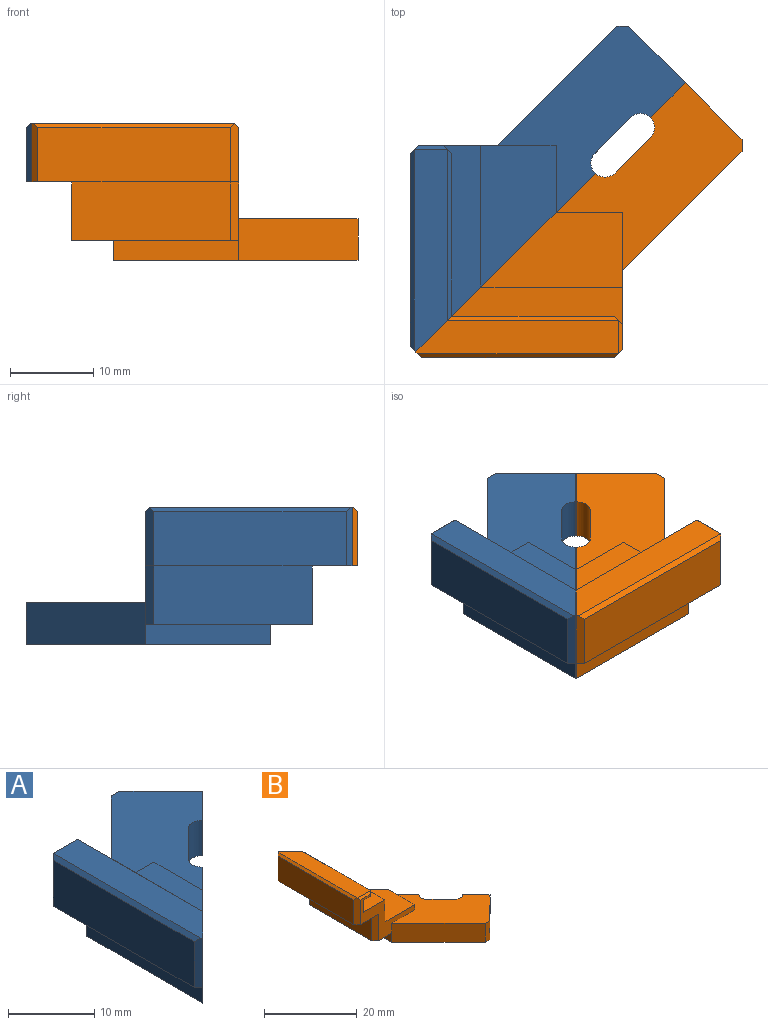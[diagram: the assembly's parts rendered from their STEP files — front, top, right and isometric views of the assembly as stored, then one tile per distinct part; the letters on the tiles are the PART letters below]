
ASSEMBLY  parts=2 mates=1
PART A: 31 faces, bbox 33x39.1x16.4 mm
  f0: plane 20x5mm, normal (0,0,-1), area 87mm2, adj f12,f17,f18,f22,f24
  f1: plane 22.5x22.29mm, normal (0,0,1), area 185.5mm2, adj f2,f14,f15,f16,f17,f19,f20,f21
  f2: plane 8x1.4mm, normal (1,0,0), area 11.2mm2, adj f1,f3,f17,f22
  f3: plane 17x9mm, normal (0,0,1), area 112.5mm2, adj f2,f4,f17,f22
  f4: plane 17x5.8mm, normal (1,0,0), area 98.6mm2, adj f3,f5,f17,f22
  f5: plane 23.5x6.5mm, normal (0,0,1), area 131.6mm2, adj f4,f6,f17,f22
  f6: plane 23.5x3.2mm, normal (1,0,0), area 75.2mm2, adj f5,f7,f17,f22
  f7: plane 23.5x3mm, normal (0,0,-1), area 65.5mm2, adj f6,f8,f17,f22,f23
  f8: plane 19.5x0.5mm, normal (1,0,0), area 9.8mm2, adj f7,f22,f23,f29
  f9: plane 24.29x4mm, normal (0,0,1), area 90mm2, adj f22,f27,f28,f29,f30
  f10: plane 23.09x6.5mm, normal (-1,0,0), area 150.1mm2, adj f11,f25,f28,f30
  f11: plane 24.79x6.5mm, normal (0,0,-1), area 124.6mm2, adj f10,f12,f17,f22,f24,f25,f30
  f12: plane 19x7mm, normal (-1,0,0), area 133mm2, adj f0,f11,f22,f24
  f13: plane 29.29x22.5mm, normal (0,0,-1), area 266mm2, adj f14,f15,f16,f18,f19,f20,f21,f22
  f14: plane 6.79x6.79mm, normal (0.71,0.71,0), area 48mm2, adj f1,f13,f21,f26
  f15: cylinder r=1.7mm len=5mm, axis (0,0,1), area 13.4mm2, adj f1,f13,f20,f22
  f16: cylinder r=1.7mm len=5mm, axis (0,0,1), area 13.4mm2, adj f1,f13,f20,f21
  f17: plane 16.5x13.5mm, normal (0,1,0), area 57.5mm2, adj f0,f1,f2,f3,f4,f5,f6,f7
  f18: plane 15x2.4mm, normal (-1,0,0), area 36mm2, adj f0,f13,f19,f22
  f19: plane 14.29x14.29mm, normal (-0.71,0.71,0), area 101.1mm2, adj f1,f13,f17,f18,f26
  f20: plane 5x4.24mm, normal (0.71,-0.71,0), area 30mm2, adj f1,f13,f15,f16
  f21: plane 5x4.18mm, normal (0.71,-0.71,0), area 29.5mm2, adj f1,f13,f14,f16
  f22: plane 21.47x21.47mm, normal (0.71,-0.71,0), area 180mm2, adj f0,f1,f2,f3,f4,f5,f6,f7
  f23: plane 1x1mm, normal (0.71,0.71,0), area 1.1mm2, adj f7,f8,f17,f27,f29
  f24: plane 7x1mm, normal (-0.71,0.71,0), area 9.9mm2, adj f0,f11,f12,f17
  f25: plane 7x1mm, normal (-0.71,0.71,0), area 9.5mm2, adj f10,f11,f17,f27,f28
  f26: plane 5x1.41mm, normal (0,1,0), area 7.1mm2, adj f1,f13,f14,f19
  f27: plane 4x0.5mm, normal (0,0.71,0.71), area 2.5mm2, adj f9,f17,f23,f25
  f28: plane 24.09x0.5mm, normal (-0.71,0,0.71), area 16.7mm2, adj f9,f10,f25,f30
  f29: plane 20.5x0.5mm, normal (0.71,0,0.71), area 14.1mm2, adj f8,f9,f22,f23
  f30: plane 7x0.71mm, normal (-0.71,-0.71,0), area 6.8mm2, adj f9,f10,f11,f22,f28
PART B: 31 faces, bbox 33x39.1x16.4 mm
  f0: plane 20x5mm, normal (0,0,-1), area 87mm2, adj f12,f17,f18,f22,f24
  f1: plane 22.5x22.29mm, normal (0,0,1), area 185.5mm2, adj f2,f14,f15,f16,f17,f19,f20,f21
  f2: plane 8x1.4mm, normal (1,0,0), area 11.2mm2, adj f1,f3,f17,f22
  f3: plane 17x9mm, normal (0,0,1), area 112.5mm2, adj f2,f4,f17,f22
  f4: plane 17x5.8mm, normal (1,0,0), area 98.6mm2, adj f3,f5,f17,f22
  f5: plane 23.5x6.5mm, normal (0,0,1), area 131.6mm2, adj f4,f6,f17,f22
  f6: plane 23.5x3.2mm, normal (1,0,0), area 75.2mm2, adj f5,f7,f17,f22
  f7: plane 23.5x3mm, normal (0,0,-1), area 65.5mm2, adj f6,f8,f17,f22,f23
  f8: plane 19.5x0.5mm, normal (1,0,0), area 9.8mm2, adj f7,f22,f23,f29
  f9: plane 24.29x4mm, normal (0,0,1), area 90mm2, adj f22,f27,f28,f29,f30
  f10: plane 23.09x6.5mm, normal (-1,0,0), area 150.1mm2, adj f11,f25,f28,f30
  f11: plane 24.79x6.5mm, normal (0,0,-1), area 124.6mm2, adj f10,f12,f17,f22,f24,f25,f30
  f12: plane 19x7mm, normal (-1,0,0), area 133mm2, adj f0,f11,f22,f24
  f13: plane 29.29x22.5mm, normal (0,0,-1), area 266mm2, adj f14,f15,f16,f18,f19,f20,f21,f22
  f14: plane 6.79x6.79mm, normal (0.71,-0.71,0), area 48mm2, adj f1,f13,f21,f26
  f15: cylinder r=1.7mm len=5mm, axis (0,0,1), area 13.4mm2, adj f1,f13,f20,f22
  f16: cylinder r=1.7mm len=5mm, axis (0,0,1), area 13.4mm2, adj f1,f13,f20,f21
  f17: plane 16.5x13.5mm, normal (0,-1,0), area 57.5mm2, adj f0,f1,f2,f3,f4,f5,f6,f7
  f18: plane 15x2.4mm, normal (-1,0,0), area 36mm2, adj f0,f13,f19,f22
  f19: plane 14.29x14.29mm, normal (-0.71,-0.71,0), area 101.1mm2, adj f1,f13,f17,f18,f26
  f20: plane 5x4.24mm, normal (0.71,0.71,0), area 30mm2, adj f1,f13,f15,f16
  f21: plane 5x4.18mm, normal (0.71,0.71,0), area 29.5mm2, adj f1,f13,f14,f16
  f22: plane 21.47x21.47mm, normal (0.71,0.71,0), area 180mm2, adj f0,f1,f2,f3,f4,f5,f6,f7
  f23: plane 1x1mm, normal (0.71,-0.71,0), area 1.1mm2, adj f7,f8,f17,f27,f29
  f24: plane 7x1mm, normal (-0.71,-0.71,0), area 9.9mm2, adj f0,f11,f12,f17
  f25: plane 7x1mm, normal (-0.71,-0.71,0), area 9.5mm2, adj f10,f11,f17,f27,f28
  f26: plane 5x1.41mm, normal (0,-1,0), area 7.1mm2, adj f1,f13,f14,f19
  f27: plane 4x0.5mm, normal (0,-0.71,0.71), area 2.5mm2, adj f9,f17,f23,f25
  f28: plane 24.09x0.5mm, normal (-0.71,0,0.71), area 16.7mm2, adj f9,f10,f25,f30
  f29: plane 20.5x0.5mm, normal (0.71,0,0.71), area 14.1mm2, adj f8,f9,f22,f23
  f30: plane 7x0.71mm, normal (-0.71,0.71,0), area 6.8mm2, adj f9,f10,f11,f22,f28
PLACE A at identity
PLACE B rot(axis=(0,0,1),90deg) t=(-60,0,0)mm
MATE fastened B.f3 <-> A.f3  axis (0,0,1) through (-8,-8,1.4)mm
